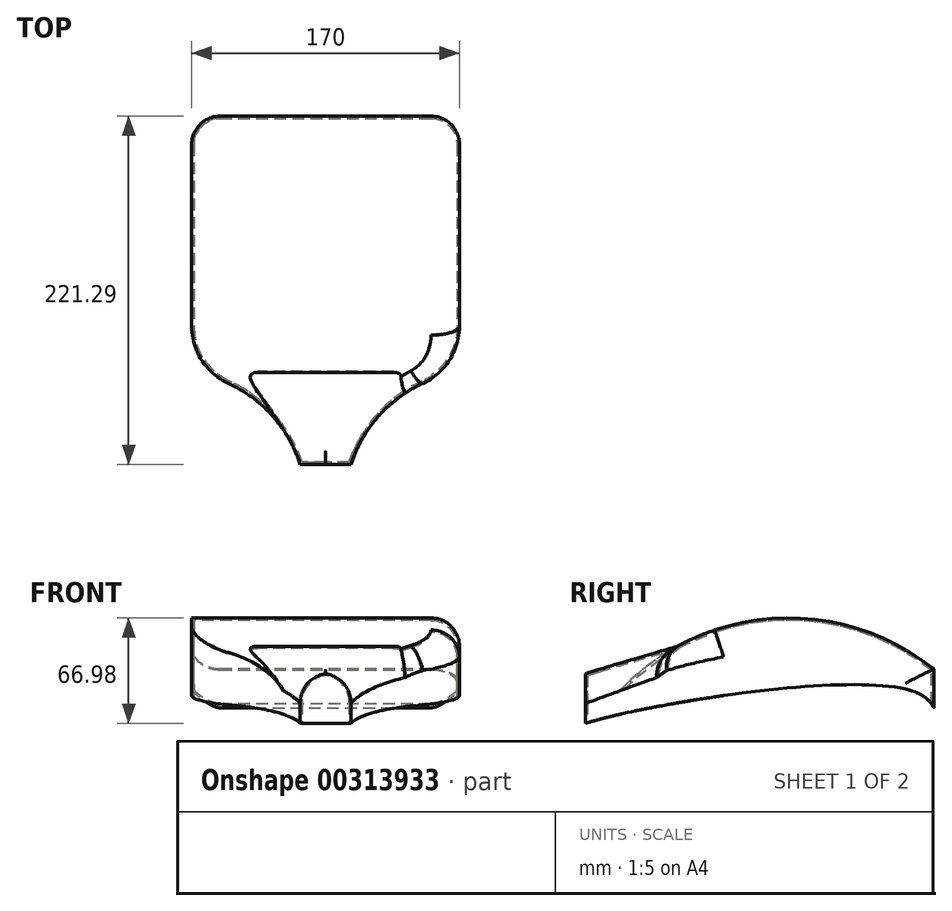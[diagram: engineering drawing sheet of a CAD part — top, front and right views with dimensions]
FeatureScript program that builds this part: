
annotation { "Feature Type Name" : "Feature", "Feature Type Description" : "" }
export const myFeature = defineFeature(function(context is Context, id is Id, definition is map)
    precondition{}
    {
        {
            var Q0;
            Q0=qCreatedBy(makeId("Top.planeOp"),FACE);
            var sketch = newSketch(context, id + "F0", { "sketchPlane" : qUnion([Q0])});
            skLineSegment(sketch, "E0", {"start": v(110.55, -100.34) * mm, "end": v(-59.45, -100.34) * mm});
            skLineSegment(sketch, "E1", {"start": v(-59.45, -100.34) * mm, "end": v(-59.45, 62.45) * mm});
            skLineSegment(sketch, "E2", {"start": v(110.55, -100.34) * mm, "end": v(110.55, 62.45) * mm});
            skArc(sketch, "E3", {"start": v(41.62, 120.95) * mm, "mid": v(67.74, 81.87) * mm, "end": v(110.55, 62.45) * mm});
            skArc(sketch, "E4.MirrorCS", {"start": v(9.41, 120.95) * mm, "mid": v(-16.68, 81.9) * mm, "end": v(-59.45, 62.45) * mm});
            skLineSegment(sketch, "E5", {"start": v(41.62, 120.95) * mm, "end": v(9.41, 120.95) * mm});
            skLineSegment(sketch, "E6", {"start": v(-59.45, 62.45) * mm, "end": v(110.55, 62.45) * mm});
            skSolve(sketch);
        }
        {
            var Q0;
            Q0=makeQuery(id+"F0.imprint","IMPRINT",FACE,{"disambiguationData":[TD([[makeQuery(id+"F0.imprint","IMPRINT",EDGE,{"derivedFrom":sQuery(id+"F0.wireOp",EDGE,"E0")}),-1.0]])]});
            extrude(context, id + "F1", {"entities" : qUnion([Q0]), "depth" : 75 * mm});
        }
        {
            var Q0;
            Q0=makeQuery(id+"F0.imprint","IMPRINT",FACE,{"disambiguationData":[TD([[makeQuery(id+"F0.imprint","IMPRINT",EDGE,{"derivedFrom":sQuery(id+"F0.wireOp",EDGE,"E3")}),-1.0]])]});
            extrude(context, id + "F2", {"entities" : qUnion([Q0]), "operationType" : NewBodyOperationType.ADD, "depth" : 57 * mm});
        }
        {
            var Q0;
            Q0=makeQuery(id+"F1.opExtrude","SWEPT_FACE",FACE,{"disambiguationData":[OSD([sQuery(id+"F0.wireOp",EDGE,"E2")])]});
            var sketch = newSketch(context, id + "F3", { "sketchPlane" : qUnion([Q0])});
            skLineSegment(sketch, "E7", {"start": v(-87.1, 0) * mm, "end": v(-102.08, 0) * mm});
            skLineSegment(sketch, "E8", {"start": v(-102.08, 0) * mm, "end": v(-102.08, 75) * mm});
            skLineSegment(sketch, "E9", {"start": v(-102.08, 75) * mm, "end": v(62.45, 75) * mm});
            skLineSegment(sketch, "E10", {"start": v(62.45, 75) * mm, "end": v(62.45, 41.97) * mm});
            skLineSegment(sketch, "E11.bottom", {"start": v(-71.58, 0) * mm, "end": v(33.42, 0) * mm});
            skLineSegment(sketch, "E11.top", {"start": v(-71.58, 60) * mm, "end": v(33.42, 60) * mm});
            skLineSegment(sketch, "E11.left", {"start": v(-71.58, 0) * mm, "end": v(-71.58, 60) * mm});
            skLineSegment(sketch, "E11.right", {"start": v(33.42, 0) * mm, "end": v(33.42, 60) * mm});
            skArc(sketch, "E12", {"start": v(62.45, 56.5) * mm, "mid": v(-21.15, 73.9) * mm, "end": v(-100.34, 41.97) * mm});
            skLineSegment(sketch, "E13", {"start": v(-100.34, 41.97) * mm, "end": v(-102.08, 41.97) * mm});
            skLineSegment(sketch, "E14", {"start": v(62.45, 56.5) * mm, "end": v(123.07, 38.66) * mm});
            skLineSegment(sketch, "E15", {"start": v(123.07, 38.66) * mm, "end": v(123.07, 75) * mm});
            skLineSegment(sketch, "E16", {"start": v(123.07, 75) * mm, "end": v(62.45, 75) * mm});
            skArc(sketch, "E17", {"start": v(-86.3, 51.96) * mm, "mid": v(-99.44, 32.09) * mm, "end": v(-102.08, 8.41) * mm});
            skSolve(sketch);
        }
        {
            var Q0;
            {var subQ0=sQuery(id+"F3.wireOp",EDGE,"E10");Q0=makeQuery(id+"F3.imprint","IMPRINT",FACE,{"disambiguationData":[TD([[makeQuery(id+"F3.imprint","IMPRINT",EDGE,{"derivedFrom":subQ0}),-1.0]])]});}
            var Q1;
            {var subQ0=sQuery(id+"F3.wireOp",EDGE,"E9");var subQ3=sQuery(id+"F3.wireOp",EDGE,"DM58jXOV-M3VW-FM4g-4zhf-81BwiUeARjpH");var subQ4=makeQuery(id+"F3.imprint","INTERSECT",VERTEX,{"disambiguationData":[OD(0.0)],"derivedFrom":[subQ0,subQ3]});Q1=makeQuery(id+"F3.imprint","IMPRINT",FACE,{"disambiguationData":[TD([[makeQuery(id+"F3.imprint","IMPRINT",EDGE,{"disambiguationData":[TD([[subQ4,1.0]])],"derivedFrom":subQ0}),-1.0]])]});}
            var Q2;
            {var subQ0=sQuery(id+"F3.wireOp",EDGE,"E14");Q2=makeQuery(id+"F3.imprint","IMPRINT",FACE,{"disambiguationData":[TD([[makeQuery(id+"F3.imprint","IMPRINT",EDGE,{"derivedFrom":subQ0}),1.0]])]});}
            extrude(context, id + "F4", {"entities" : qUnion([Q0, Q1, Q2]), "operationType" : NewBodyOperationType.REMOVE, "oppositeDirection" : true, "depth" : 200 * mm});
        }
        {
            var Q0;
            Q0=makeQuery(id+"F1.opExtrude","SWEPT_BODY",BODY,{"disambiguationData":[OSD([sQuery(id+"F0.wireOp",EDGE,"E0"),sQuery(id+"F0.wireOp",EDGE,"E1"),sQuery(id+"F0.wireOp",EDGE,"E2"),sQuery(id+"F0.wireOp",EDGE,"E3"),sQuery(id+"F0.wireOp",EDGE,"E4.MirrorCS"),sQuery(id+"F0.wireOp",EDGE,"E5")])]});
            var Q1;
            Q1=makeQuery(id+"F4.boolean.opBoolean","SPLIT",EDGE,{"derivedFrom":makeQuery(id+"F1.opExtrude","SWEPT_EDGE",EDGE,{"disambiguationData":[OSD([sQuery(id+"F0.wireOp",EDGE,"E2"),sQuery(id+"F0.wireOp",EDGE,"E3")])]})});
            transform(context, id + "F5", {"entities" : qUnion([Q0]), "transformType" : TransformType.ROTATION, "transformAxis" : qUnion([Q1]), "angle" : 180 * degree, "makeCopy" : false});
        }
        {
            var Q0;
            Q0=makeQuery(id+"F1.opExtrude","SWEPT_FACE",FACE,{"disambiguationData":[OSD([sQuery(id+"F0.wireOp",EDGE,"E1")])]});
            var sketch = newSketch(context, id + "F6", { "sketchPlane" : qUnion([Q0])});
            skFitSpline(sketch, "E18", {"points": [v(223.88, 5.94) * mm, v(213.4, 27.46) * mm, v(-5.4, 3.31) * mm, v(158.12, 1.38) * mm, v(223.88, 5.94) * mm]});
            skLineSegment(sketch, "E19", {"start": v(-5.4, 3.31) * mm, "end": v(-5.4, -10.26) * mm});
            skLineSegment(sketch, "E20", {"start": v(-5.4, -10.26) * mm, "end": v(228.25, -10.26) * mm});
            skLineSegment(sketch, "E21", {"start": v(228.25, -10.26) * mm, "end": v(226.11, 12.2) * mm});
            skSolve(sketch);
        }
        {
            var Q0;
            {var subQ0=sQuery(id+"F6.wireOp",EDGE,"E18");var subQ1=sQuery(id+"F0.wireOp",EDGE,"E1");var subQ2=makeQuery(id+"F1.opExtrude","CAP_EDGE",EDGE,{"disambiguationData":[OSD([subQ1])],"isStart":true});var subQ10=makeQuery(id+"F6.imprint","INTERSECT",VERTEX,{"disambiguationData":[OD(0.0)],"derivedFrom":[subQ2,subQ0]});Q0=makeQuery(id+"F6.imprint","IMPRINT",FACE,{"disambiguationData":[TD([[makeQuery(id+"F6.imprint","IMPRINT",EDGE,{"disambiguationData":[TD([[subQ10,-1.0]])],"derivedFrom":subQ0}),1.0]])]});}
            var Q1;
            {var subQ0=sQuery(id+"F6.wireOp",EDGE,"E18");var subQ1=sQuery(id+"F0.wireOp",EDGE,"E1");var subQ5=makeQuery(id+"F1.opExtrude","CAP_EDGE",EDGE,{"disambiguationData":[OSD([subQ1])],"isStart":true});var subQ6=makeQuery(id+"F6.imprint","INTERSECT",VERTEX,{"disambiguationData":[OD(0.0)],"derivedFrom":[subQ5,subQ0]});Q1=makeQuery(id+"F6.imprint","IMPRINT",FACE,{"disambiguationData":[TD([[makeQuery(id+"F6.imprint","IMPRINT",EDGE,{"disambiguationData":[TD([[subQ6,1.0]])],"derivedFrom":subQ0}),1.0]])]});}
            extrude(context, id + "F7", {"entities" : qUnion([Q0, Q1]), "operationType" : NewBodyOperationType.REMOVE, "oppositeDirection" : true, "depth" : 200 * mm});
        }
        {
            var Q0;
            Q0=makeQuery(id+"F4.boolean.opBoolean","INTERSECT",EDGE,{"derivedFrom":[makeQuery(id+"F2.opExtrude","SWEPT_FACE",FACE,{"disambiguationData":[OSD([sQuery(id+"F0.wireOp",EDGE,"E4.MirrorCS")])]}),makeQuery(id+"F4.opExtrude","SWEPT_FACE",FACE,{"disambiguationData":[OSD([sQuery(id+"F3.wireOp",EDGE,"E14")])]})]});
            var Q1;
            Q1=makeQuery(id+"F4.boolean.opBoolean","INTERSECT",EDGE,{"derivedFrom":[makeQuery(id+"F2.opExtrude","SWEPT_FACE",FACE,{"disambiguationData":[OSD([sQuery(id+"F0.wireOp",EDGE,"E3")])]}),makeQuery(id+"F4.opExtrude","SWEPT_FACE",FACE,{"disambiguationData":[OSD([sQuery(id+"F3.wireOp",EDGE,"E14")])]})]});
            fillet(context, id + "F8", {"entities" : qUnion([Q0, Q1]), "radius" : 20 * mm, "tangentPropagation" : true, "allowEdgeOverflow" : false});
        }
        {
            var Q0;
            {var subQ0=sQuery(id+"F0.wireOp",EDGE,"E6");var subQ1=sQuery(id+"F0.wireOp",EDGE,"E4.MirrorCS");var subQ2=sQuery(id+"F0.wireOp",EDGE,"E1");Q0=makeQuery(id+"F2.boolean.opBoolean","MERGE",EDGE,{"derivedFrom":[makeQuery(id+"F1.opExtrude","SWEPT_EDGE",EDGE,{"disambiguationData":[OSD([subQ2,subQ1,subQ0])]}),makeQuery(id+"F2.opExtrude","SWEPT_EDGE",EDGE,{"disambiguationData":[OSD([subQ2,subQ1,subQ0])]})]});}
            var Q1;
            {var subQ0=sQuery(id+"F0.wireOp",EDGE,"E6");var subQ1=sQuery(id+"F0.wireOp",EDGE,"E3");var subQ2=sQuery(id+"F0.wireOp",EDGE,"E2");Q1=makeQuery(id+"F2.boolean.opBoolean","MERGE",EDGE,{"derivedFrom":[makeQuery(id+"F1.opExtrude","SWEPT_EDGE",EDGE,{"disambiguationData":[OSD([subQ2,subQ1,subQ0])]}),makeQuery(id+"F2.opExtrude","SWEPT_EDGE",EDGE,{"disambiguationData":[OSD([subQ2,subQ1,subQ0])]})]});}
            fillet(context, id + "F9", {"entities" : qUnion([Q0, Q1]), "radius" : 40 * mm, "tangentPropagation" : true, "allowEdgeOverflow" : false});
        }
        {
            var Q0;
            {var subQ0=sQuery(id+"F6.wireOp",EDGE,"E18");var subQ1=sQuery(id+"F0.wireOp",EDGE,"E1");var subQ4=makeQuery(id+"F1.opExtrude","CAP_EDGE",EDGE,{"disambiguationData":[OSD([subQ1])],"isStart":true});var subQ5=makeQuery(id+"F6.imprint","INTERSECT",VERTEX,{"disambiguationData":[OD(2.0)],"derivedFrom":[subQ4,subQ0]});Q0=makeQuery(id+"F6.imprint","IMPRINT",FACE,{"disambiguationData":[TD([[makeQuery(id+"F6.imprint","IMPRINT",EDGE,{"disambiguationData":[TD([[subQ5,-1.0]])],"derivedFrom":subQ0}),-1.0]])]});}
            var Q1;
            {var subQ0=sQuery(id+"F6.wireOp",EDGE,"E18");var subQ1=makeQuery(id+"F1.opExtrude","CAP_EDGE",EDGE,{"disambiguationData":[OSD([sQuery(id+"F0.wireOp",EDGE,"E1")])],"isStart":true});var subQ2=makeQuery(id+"F6.imprint","INTERSECT",VERTEX,{"disambiguationData":[OD(0.0)],"derivedFrom":[subQ1,subQ0]});Q1=makeQuery(id+"F6.imprint","IMPRINT",FACE,{"disambiguationData":[TD([[makeQuery(id+"F6.imprint","IMPRINT",EDGE,{"disambiguationData":[TD([[subQ2,-1.0]])],"derivedFrom":subQ0}),-1.0]])]});}
            extrude(context, id + "F10", {"entities" : qUnion([Q0, Q1]), "operationType" : NewBodyOperationType.REMOVE, "oppositeDirection" : true, "depth" : 180 * mm});
        }
        {
            var Q0;
            {var subQ0=sQuery(id+"F0.wireOp",EDGE,"E0");var subQ2=sQuery(id+"F0.wireOp",EDGE,"E1");var subQ7=makeQuery(id+"F1.opExtrude","SWEPT_EDGE",EDGE,{"disambiguationData":[OSD([subQ0,subQ2])]});Q0=makeQuery(id+"F7.boolean.opBoolean","SPLIT",EDGE,{"disambiguationData":[TD([makeQuery(id+"F4.boolean.opBoolean","COPY",FACE,{"derivedFrom":makeQuery(id+"F4.opExtrude","SWEPT_FACE",FACE,{"disambiguationData":[OSD([sQuery(id+"F3.wireOp",EDGE,"E12")])]})})])],"derivedFrom":subQ7});}
            var Q1;
            {var subQ0=sQuery(id+"F0.wireOp",EDGE,"E0");var subQ6=sQuery(id+"F0.wireOp",EDGE,"E2");Q1=makeQuery(id+"F7.boolean.opBoolean","SPLIT",EDGE,{"disambiguationData":[TD([makeQuery(id+"F4.boolean.opBoolean","COPY",FACE,{"derivedFrom":makeQuery(id+"F4.opExtrude","SWEPT_FACE",FACE,{"disambiguationData":[OSD([sQuery(id+"F3.wireOp",EDGE,"E12")])]})})])],"derivedFrom":makeQuery(id+"F1.opExtrude","SWEPT_EDGE",EDGE,{"disambiguationData":[OSD([subQ0,subQ6])]})});}
            var Q2;
            Q2=makeQuery(id+"F4.boolean.opBoolean","COPY",EDGE,{"derivedFrom":makeQuery(id+"F4.opExtrude","CAP_EDGE",EDGE,{"disambiguationData":[OSD([sQuery(id+"F3.wireOp",EDGE,"E12")])],"isStart":true})});
            var Q3;
            Q3=makeQuery(id+"F4.boolean.opBoolean","INTERSECT",EDGE,{"derivedFrom":[makeQuery(id+"F1.opExtrude","SWEPT_FACE",FACE,{"disambiguationData":[OSD([sQuery(id+"F0.wireOp",EDGE,"E1")])]}),makeQuery(id+"F4.opExtrude","SWEPT_FACE",FACE,{"disambiguationData":[OSD([sQuery(id+"F3.wireOp",EDGE,"E12")])]})]});
            var Q4;
            Q4=makeQuery(id+"F4.boolean.opBoolean","COPY",EDGE,{"derivedFrom":makeQuery(id+"F4.opExtrude","SWEPT_EDGE",EDGE,{"disambiguationData":[OSD([sQuery(id+"F0.wireOp",EDGE,"E0"),sQuery(id+"F0.wireOp",EDGE,"E2"),sQuery(id+"F3.wireOp",EDGE,"E12"),sQuery(id+"F3.wireOp",EDGE,"E13")])]})});
            fillet(context, id + "F11", {"entities" : qUnion([Q0, Q1, Q2, Q3, Q4]), "radius" : 18 * mm, "tangentPropagation" : true, "allowEdgeOverflow" : false});
        }
        {
            var Q0;
            {var subQ0=sQuery(id+"F6.wireOp",EDGE,"E18");var subQ3=sQuery(id+"F0.wireOp",EDGE,"E1");Q0=makeQuery(id+"F7.boolean.opBoolean","COPY",FACE,{"derivedFrom":makeQuery(id+"F7.opExtrude","SWEPT_FACE",FACE,{"disambiguationData":[OSD([subQ0]),TDD([makeQuery(id+"F6.imprint","IMPRINT",EDGE,{"disambiguationData":[TD([[makeQuery(id+"F6.imprint","INTERSECT",VERTEX,{"disambiguationData":[OD(0.0)],"derivedFrom":[makeQuery(id+"F1.opExtrude","SWEPT_EDGE",EDGE,{"disambiguationData":[OSD([sQuery(id+"F0.wireOp",EDGE,"E0"),subQ3])]}),subQ0]}),-1.0]])],"derivedFrom":subQ0}),makeQuery(id+"F6.imprint","IMPRINT",EDGE,{"disambiguationData":[TD([[makeQuery(id+"F6.imprint","INTERSECT",VERTEX,{"disambiguationData":[OD(0.0)],"derivedFrom":[subQ0,sQuery(id+"F6.wireOp",EDGE,"E19")]}),1.0]])],"derivedFrom":subQ0})])]})});}
            shell(context, id + "F12", {"entities" : qUnion([Q0]), "thickness" : 1.5 * mm});
        }
    });
